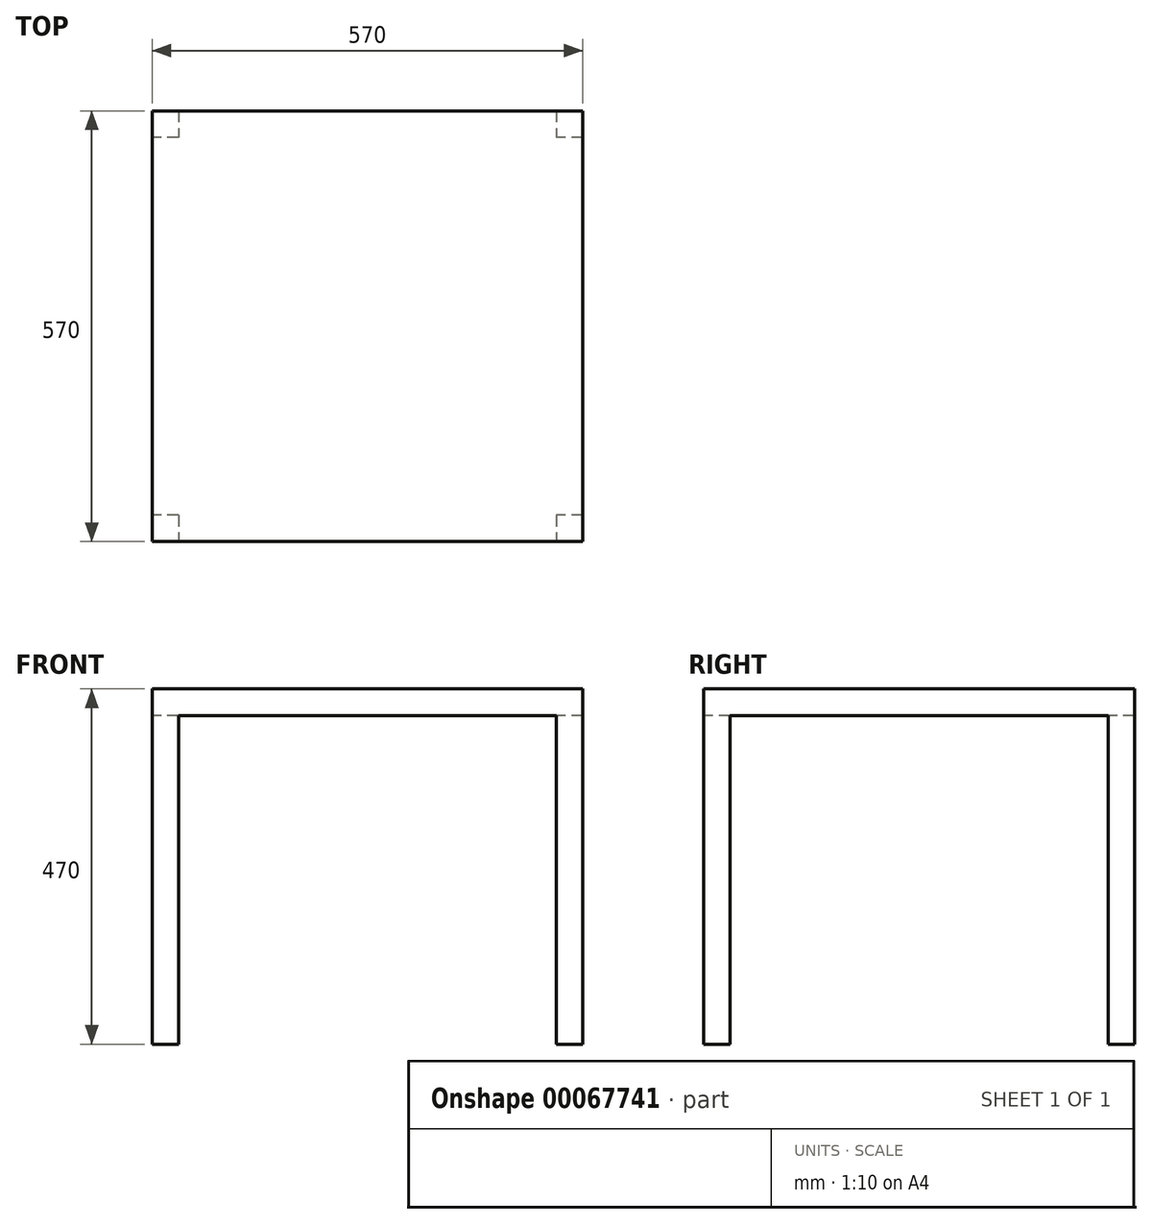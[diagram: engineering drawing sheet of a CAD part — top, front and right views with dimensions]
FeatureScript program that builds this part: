
annotation { "Feature Type Name" : "Feature", "Feature Type Description" : "" }
export const myFeature = defineFeature(function(context is Context, id is Id, definition is map)
    precondition{}
    {
        {
            var Q0;
            Q0=qCreatedBy(makeId("Front.planeOp"),FACE);
            var sketch = newSketch(context, id + "F0", { "sketchPlane" : qUnion([Q0])});
            skLineSegment(sketch, "E0", {"start": v(0, 0) * mm, "end": v(570, 0) * mm});
            skLineSegment(sketch, "E1", {"start": v(570, 0) * mm, "end": v(570, 470) * mm});
            skLineSegment(sketch, "E2", {"start": v(570, 470) * mm, "end": v(0, 470) * mm});
            skLineSegment(sketch, "E3", {"start": v(0, 470) * mm, "end": v(0, 0) * mm});
            skSolve(sketch);
        }
        {
            var Q0;
            Q0=makeQuery(id+"F0.imprint","IMPRINT",FACE,{"disambiguationData":[TD([[makeQuery(id+"F0.imprint","IMPRINT",EDGE,{"derivedFrom":sQuery(id+"F0.wireOp",EDGE,"E0")}),1.0]])]});
            extrude(context, id + "F1", {"entities" : qUnion([Q0]), "depth" : 570 * mm});
        }
        {
            var Q0;
            Q0=makeQuery(id+"F1.opExtrude","CAP_FACE",FACE,{"disambiguationData":[OSD([sQuery(id+"F0.wireOp",EDGE,"E0"),sQuery(id+"F0.wireOp",EDGE,"E1"),sQuery(id+"F0.wireOp",EDGE,"E2"),sQuery(id+"F0.wireOp",EDGE,"E3")])],"isStart":false});
            var sketch = newSketch(context, id + "F2", { "sketchPlane" : qUnion([Q0])});
            skLineSegment(sketch, "E4.bottom", {"start": v(35, 0) * mm, "end": v(535, 0) * mm});
            skLineSegment(sketch, "E4.top", {"start": v(35, 435) * mm, "end": v(535, 435) * mm});
            skLineSegment(sketch, "E4.left", {"start": v(35, 0) * mm, "end": v(35, 435) * mm});
            skLineSegment(sketch, "E4.right", {"start": v(535, 0) * mm, "end": v(535, 435) * mm});
            skSolve(sketch);
        }
        {
            var Q0;
            Q0=makeQuery(id+"F2.imprint","IMPRINT",FACE,{"disambiguationData":[TD([[makeQuery(id+"F2.imprint","IMPRINT",EDGE,{"derivedFrom":sQuery(id+"F2.wireOp",EDGE,"E4.bottom")}),1.0]])]});
            extrude(context, id + "F3", {"entities" : qUnion([Q0]), "operationType" : NewBodyOperationType.REMOVE, "endBound" : BoundingType.THROUGH_ALL, "oppositeDirection" : true, "depth" : 25 * mm});
        }
        {
            var Q0;
            Q0=makeQuery(id+"F1.opExtrude","SWEPT_FACE",FACE,{"disambiguationData":[OSD([sQuery(id+"F0.wireOp",EDGE,"E3")])]});
            var sketch = newSketch(context, id + "F4", { "sketchPlane" : qUnion([Q0])});
            skLineSegment(sketch, "E5.bottom", {"start": v(35, 0) * mm, "end": v(535, 0) * mm});
            skLineSegment(sketch, "E5.top", {"start": v(35, 435) * mm, "end": v(535, 435) * mm});
            skLineSegment(sketch, "E5.left", {"start": v(35, 0) * mm, "end": v(35, 435) * mm});
            skLineSegment(sketch, "E5.right", {"start": v(535, 0) * mm, "end": v(535, 435) * mm});
            skSolve(sketch);
        }
        {
            var Q0;
            Q0=makeQuery(id+"F4.imprint","IMPRINT",FACE,{"disambiguationData":[TD([[makeQuery(id+"F4.imprint","IMPRINT",EDGE,{"derivedFrom":sQuery(id+"F4.wireOp",EDGE,"E5.bottom")}),-1.0]])]});
            extrude(context, id + "F5", {"entities" : qUnion([Q0]), "operationType" : NewBodyOperationType.REMOVE, "endBound" : BoundingType.THROUGH_ALL, "oppositeDirection" : true, "depth" : 25 * mm});
        }
    });
